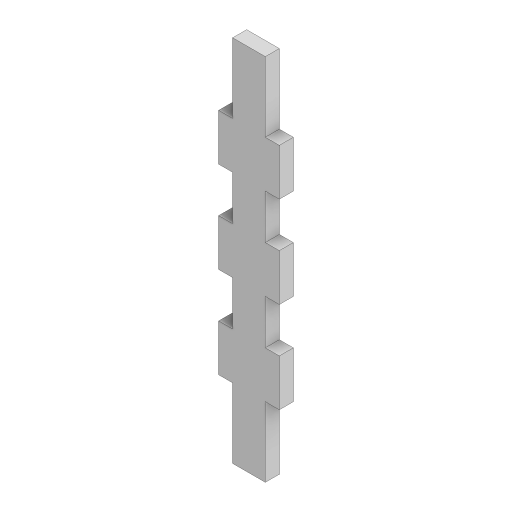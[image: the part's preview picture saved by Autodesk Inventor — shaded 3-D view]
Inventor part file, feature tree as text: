
AUTODESK INVENTOR PART (.ipt)
format: ipt  version: 2023.3 (Build 273359000, 359)  size: 126,464 bytes
history: native  units: mm
features: extrude x1, sketch x1
ambient origin geometry x8: Origin, YZ Plane, XZ Plane, XY Plane, X Axis, Y Axis, Z Axis, Center Point
bodies: Solid1 (feature_tree)
feature tree (2):
  extrude  "Extrusion1"  Depth=13.0mm
  sketch  "Sketch1"  dims[d0=79.0mm d1=13.0mm d2=3.0mm d3=3.0mm d4=3.0mm d5=10.0mm d6=4.0mm d7=10.0mm d8=10.0mm d9=3.0mm d10=0.0mm]
